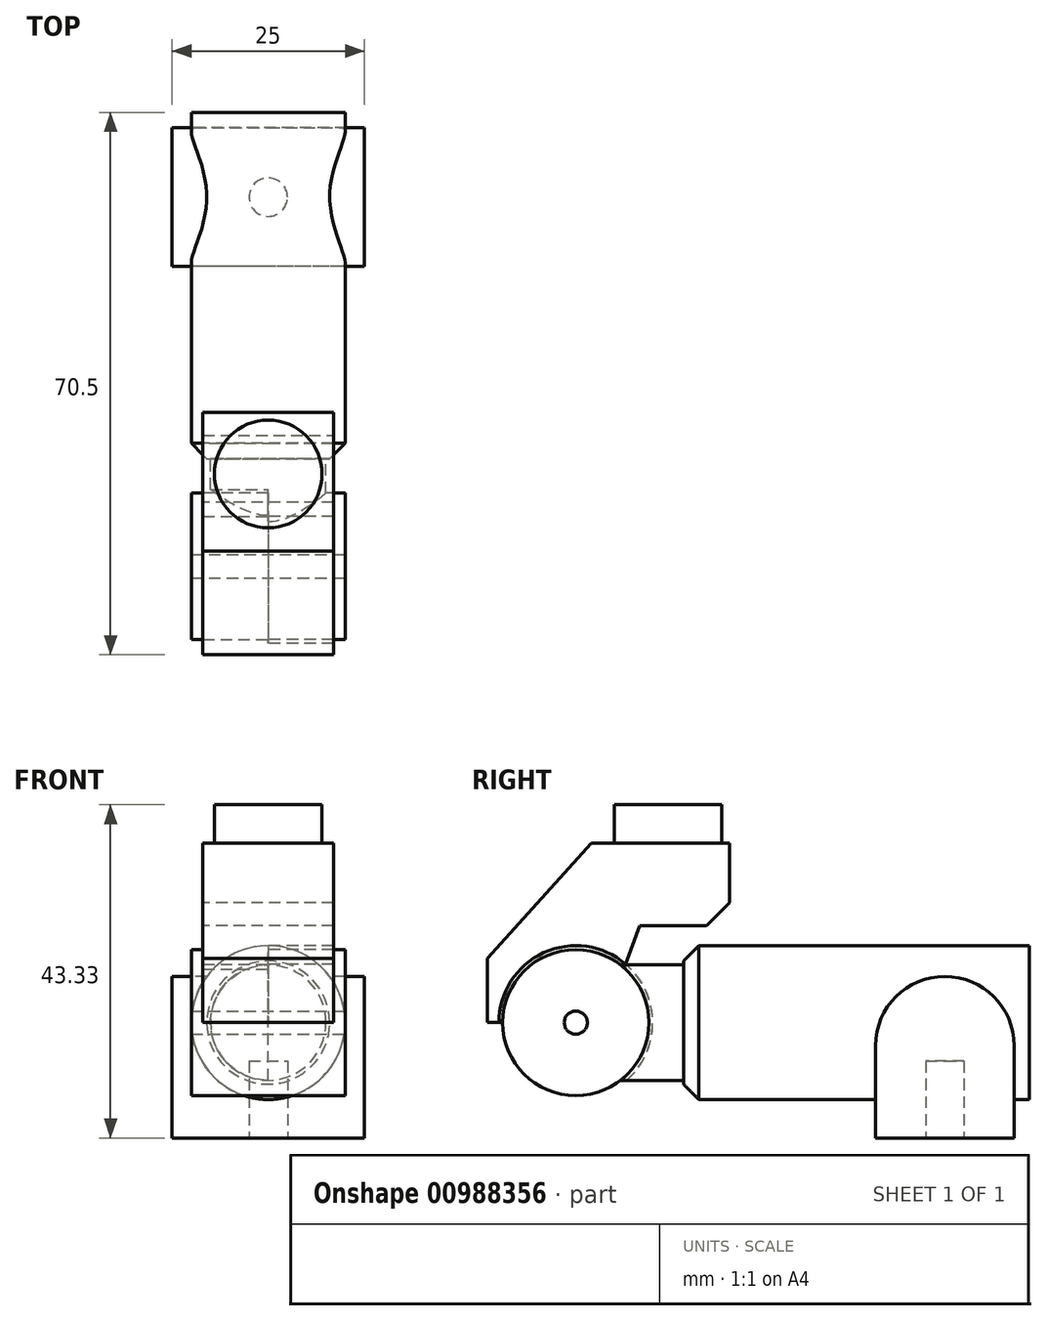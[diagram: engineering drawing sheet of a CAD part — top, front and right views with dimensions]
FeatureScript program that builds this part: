
annotation { "Feature Type Name" : "Feature", "Feature Type Description" : "" }
export const myFeature = defineFeature(function(context is Context, id is Id, definition is map)
    precondition{}
    {
        {
            var Q0;
            Q0=qCreatedBy(makeId("Front.planeOp"),FACE);
            var sketch = newSketch(context, id + "F0", { "sketchPlane" : qUnion([Q0])});
            skCircle(sketch, "E0", {"center": v(0, 0) * mm, "radius": 10 * mm});
            skSolve(sketch);
        }
        {
            var Q0;
            Q0=qSketchRegion(id+"F0",true);
            extrude(context, id + "F1", {"entities" : qUnion([Q0]), "endBound" : BoundingType.SYMMETRIC, "depth" : 45 * mm, "offsetDistance" : 25 * mm});
        }
        {
            var Q0;
            Q0=makeQuery(id+"F1.opExtrude","CAP_FACE",FACE,{"disambiguationData":[OSD([sQuery(id+"F0.wireOp",EDGE,"E0")])],"isStart":false});
            var sketch = newSketch(context, id + "F2", { "sketchPlane" : qUnion([Q0])});
            skCircle(sketch, "E1", {"center": v(0, 0) * mm, "radius": 7.5 * mm});
            skSolve(sketch);
        }
        {
            var Q0;
            Q0=qSketchRegion(id+"F2",true);
            extrude(context, id + "F3", {"entities" : qUnion([Q0]), "operationType" : NewBodyOperationType.ADD, "depth" : 10 * mm, "offsetDistance" : 25 * mm});
        }
        {
            var Q0;
            Q0=qCreatedBy(makeId("Right.planeOp"),FACE);
            var sketch = newSketch(context, id + "F4", { "sketchPlane" : qUnion([Q0])});
            skCircle(sketch, "E2", {"center": v(-36.5, 0) * mm, "radius": 9.5 * mm});
            skSolve(sketch);
        }
        {
            var Q0;
            Q0=qSketchRegion(id+"F4",true);
            extrude(context, id + "F5", {"entities" : qUnion([Q0]), "operationType" : NewBodyOperationType.ADD, "endBound" : BoundingType.SYMMETRIC, "depth" : 20 * mm, "offsetDistance" : 25 * mm});
        }
        {
            var Q0;
            Q0=makeQuery(id+"F1.opExtrude","CAP_EDGE",EDGE,{"disambiguationData":[OSD([sQuery(id+"F0.wireOp",EDGE,"E0")])],"isStart":false});
            chamfer(context, id + "F6", {"entities" : qUnion([Q0]), "width" : 2 * mm, "tangentPropagation" : true});
        }
        {
            var Q0;
            Q0=qCreatedBy(makeId("Right.planeOp"),FACE);
            var sketch = newSketch(context, id + "F7", { "sketchPlane" : qUnion([Q0])});
            skArc(sketch, "E3", {"start": v(-30, 7.6) * mm, "mid": v(-40.68, 9.08) * mm, "end": v(-46.5, 0) * mm});
            skLineSegment(sketch, "E4", {"start": v(-46.5, 0) * mm, "end": v(-46.5, 10) * mm});
            skLineSegment(sketch, "E5", {"start": v(-46.5, 10) * mm, "end": v(-34.5, 23.33) * mm});
            skLineSegment(sketch, "E6", {"start": v(-34.5, 23.33) * mm, "end": v(-16.5, 23.33) * mm});
            skLineSegment(sketch, "E7", {"start": v(-16.5, 23.33) * mm, "end": v(-16.5, 12.6) * mm});
            skLineSegment(sketch, "E8", {"start": v(-16.5, 12.6) * mm, "end": v(-28.18, 12.6) * mm});
            skLineSegment(sketch, "E9", {"start": v(-28.18, 12.6) * mm, "end": v(-30, 7.6) * mm});
            skSolve(sketch);
        }
        {
            var Q0;
            Q0=qSketchRegion(id+"F7",true);
            extrude(context, id + "F8", {"entities" : qUnion([Q0]), "endBound" : BoundingType.SYMMETRIC, "depth" : 17 * mm, "offsetDistance" : 25 * mm});
        }
        {
            var Q0;
            Q0=makeQuery(id+"F8.opExtrude","SWEPT_FACE",FACE,{"disambiguationData":[OSD([sQuery(id+"F7.wireOp",EDGE,"E6")])]});
            var sketch = newSketch(context, id + "F9", { "sketchPlane" : qUnion([Q0])});
            skCircle(sketch, "E10", {"center": v(0, -24.5) * mm, "radius": 7 * mm});
            skSolve(sketch);
        }
        {
            var Q0;
            Q0=qSketchRegion(id+"F9",true);
            extrude(context, id + "F10", {"entities" : qUnion([Q0]), "operationType" : NewBodyOperationType.ADD, "depth" : 5 * mm, "offsetDistance" : 25 * mm});
        }
        {
            var Q0;
            Q0=qCreatedBy(makeId("Right.planeOp"),FACE);
            var sketch = newSketch(context, id + "F11", { "sketchPlane" : qUnion([Q0])});
            skCircle(sketch, "E11", {"center": v(-36.5, 0) * mm, "radius": 10 * mm});
            skSolve(sketch);
        }
        {
            var Q0;
            Q0=qSketchRegion(id+"F11",true);
            extrude(context, id + "F12", {"entities" : qUnion([Q0]), "operationType" : NewBodyOperationType.REMOVE, "oppositeDirection" : true, "depth" : 25 * mm, "offsetDistance" : 25 * mm});
        }
        {
            var Q0;
            Q0=qCreatedBy(makeId("Right.planeOp"),FACE);
            var sketch = newSketch(context, id + "F13", { "sketchPlane" : qUnion([Q0])});
            skCircle(sketch, "E12", {"center": v(-36.5, 0) * mm, "radius": 9.5 * mm});
            skSolve(sketch);
        }
        {
            var Q0;
            Q0=qSketchRegion(id+"F13",true);
            extrude(context, id + "F14", {"entities" : qUnion([Q0]), "oppositeDirection" : true, "depth" : 10 * mm, "offsetDistance" : 25 * mm});
        }
        {
            var Q0;
            Q0=qCreatedBy(makeId("Right.planeOp"),FACE);
            var sketch = newSketch(context, id + "F15", { "sketchPlane" : qUnion([Q0])});
            skArc(sketch, "E13", {"start": v(-30, 7.6) * mm, "mid": v(-40.68, 9.08) * mm, "end": v(-46.5, 0) * mm});
            skArc(sketch, "E14", {"start": v(-46, 0) * mm, "mid": v(-32.73, -8.72) * mm, "end": v(-30, 6.93) * mm});
            skLineSegment(sketch, "E15", {"start": v(-30, 7.6) * mm, "end": v(-30, 6.93) * mm});
            skLineSegment(sketch, "E16", {"start": v(-46.5, 0) * mm, "end": v(-46, 0) * mm});
            skSolve(sketch);
        }
        {
            var Q0;
            Q0=qSketchRegion(id+"F15",true);
            var Q1;
            Q1=makeQuery(id+"F8.opExtrude","CAP_FACE",FACE,{"disambiguationData":[OSD([sQuery(id+"F7.wireOp",EDGE,"E3"),sQuery(id+"F7.wireOp",EDGE,"E4"),sQuery(id+"F7.wireOp",EDGE,"E5"),sQuery(id+"F7.wireOp",EDGE,"E6"),sQuery(id+"F7.wireOp",EDGE,"E7"),sQuery(id+"F7.wireOp",EDGE,"E8"),sQuery(id+"F7.wireOp",EDGE,"E9")])],"isStart":true});
            extrude(context, id + "F16", {"entities" : qUnion([Q0]), "operationType" : NewBodyOperationType.ADD, "endBound" : BoundingType.UP_TO_SURFACE, "oppositeDirection" : true, "depth" : 25 * mm, "endBoundEntityFace" : qUnion([Q1]), "offsetDistance" : 25 * mm});
        }
        {
            var Q0;
            Q0=makeQuery(id+"F8.opExtrude","SWEPT_FACE",FACE,{"disambiguationData":[OSD([sQuery(id+"F7.wireOp",EDGE,"E4")])]});
            extrude(context, id + "F17", {"entities" : qUnion([Q0]), "operationType" : NewBodyOperationType.ADD, "depth" : 1.5 * mm, "offsetDistance" : 25 * mm});
        }
        {
            var Q0;
            Q0=qCreatedBy(makeId("Right.planeOp"),FACE);
            var sketch = newSketch(context, id + "F18", { "sketchPlane" : qUnion([Q0])});
            skLineSegment(sketch, "E17", {"start": v(-46.5, 10) * mm, "end": v(-51.5, 4.45) * mm});
            skLineSegment(sketch, "E18", {"start": v(-51.5, 4.45) * mm, "end": v(-51.5, 10) * mm});
            skLineSegment(sketch, "E19", {"start": v(-51.5, 10) * mm, "end": v(-46.5, 10) * mm});
            skSolve(sketch);
        }
        {
            var Q0;
            Q0=qSketchRegion(id+"F18",true);
            extrude(context, id + "F19", {"entities" : qUnion([Q0]), "operationType" : NewBodyOperationType.REMOVE, "endBound" : BoundingType.SYMMETRIC, "oppositeDirection" : true, "depth" : 25 * mm, "offsetDistance" : 25 * mm});
        }
        {
            var Q0;
            Q0=qCreatedBy(makeId("Right.planeOp"),FACE);
            var sketch = newSketch(context, id + "F20", { "sketchPlane" : qUnion([Q0])});
            skCircle(sketch, "E20", {"center": v(-36.5, 0) * mm, "radius": 1.5 * mm});
            skSolve(sketch);
        }
        {
            var Q0;
            Q0=qSketchRegion(id+"F20",true);
            extrude(context, id + "F21", {"entities" : qUnion([Q0]), "operationType" : NewBodyOperationType.REMOVE, "endBound" : BoundingType.SYMMETRIC, "oppositeDirection" : true, "depth" : 25 * mm, "offsetDistance" : 25 * mm});
        }
        {
            var Q0;
            Q0=qCreatedBy(makeId("Right.planeOp"),FACE);
            var sketch = newSketch(context, id + "F22", { "sketchPlane" : qUnion([Q0])});
            skArc(sketch, "E21", {"start": v(20.5, -3) * mm, "mid": v(11.5, 6) * mm, "end": v(2.5, -3) * mm});
            skLineSegment(sketch, "E22", {"start": v(2.5, -3) * mm, "end": v(2.5, -15) * mm});
            skLineSegment(sketch, "E23", {"start": v(2.5, -15) * mm, "end": v(20.5, -15) * mm});
            skLineSegment(sketch, "E24", {"start": v(20.5, -15) * mm, "end": v(20.5, -3) * mm});
            skSolve(sketch);
        }
        {
            var Q0;
            Q0=qSketchRegion(id+"F22",true);
            extrude(context, id + "F23", {"entities" : qUnion([Q0]), "operationType" : NewBodyOperationType.ADD, "endBound" : BoundingType.SYMMETRIC, "depth" : 25 * mm, "offsetDistance" : 25 * mm});
        }
        {
            var Q0;
            Q0=makeQuery(id+"F23.opExtrude","SWEPT_FACE",FACE,{"disambiguationData":[OSD([sQuery(id+"F22.wireOp",EDGE,"E23")])]});
            var sketch = newSketch(context, id + "F24", { "sketchPlane" : qUnion([Q0])});
            skCircle(sketch, "E25", {"center": v(0, -11.5) * mm, "radius": 2.5 * mm});
            skSolve(sketch);
        }
        {
            var Q0;
            Q0=qSketchRegion(id+"F24",true);
            extrude(context, id + "F25", {"entities" : qUnion([Q0]), "operationType" : NewBodyOperationType.REMOVE, "oppositeDirection" : true, "depth" : 10 * mm, "offsetDistance" : 25 * mm});
        }
        {
            var Q0;
            Q0=makeQuery(id+"F8.opExtrude","SWEPT_EDGE",EDGE,{"disambiguationData":[OSD([sQuery(id+"F7.wireOp",EDGE,"E7"),sQuery(id+"F7.wireOp",EDGE,"E8")])]});
            chamfer(context, id + "F26", {"entities" : qUnion([Q0]), "width" : 3 * mm, "tangentPropagation" : true});
        }
    });
